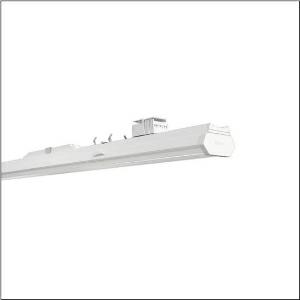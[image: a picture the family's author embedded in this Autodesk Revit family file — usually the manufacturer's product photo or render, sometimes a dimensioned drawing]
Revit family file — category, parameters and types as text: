
# Revit family: licross_r__11_protected_mo_51td11dn495g_7274
name_source: partatom
category: Lighting Fixtures
units: mm (PartAtom-declared; Revit-internal decimal feet)

## family parameters
Cut with Voids When Loaded = No
Host = Face
Light Source = No
Part Type = Normal
Room Calculation Point = No
Round Connector Dimension = Use Diameter
Shared = No

## types (1)
- --- (1 x LED, 9930 lm, 57.1 W, 4000K)
    Apparent Load = 57 VA
    CIE Flux Codes = 83 94 98 100 100
    Color Rendering = 80
    Color Temperature = 4000K
    Default Elevation = 1800 mm
    Description = Licross® 11 Protected MO, luminaire insert, of sheet steel, galvanised, coil coated, white, length: 1.500mm, width: 90mm, height: 101mm, LED rated luminous flux: 9.930lm, light colour: 840, control gear: DALI 2, control gear: ECG DALI, with plug, 5-pole, with phase selection, mains connection: 220..240V, AC, 50/60Hz, halogen-free wiring, primary light control with lens, of plastic, primary optical cover: cover, of PMMA, light emission: direct with ceiling illumination distribution, primary light characteristic: symmetric, protection rating (complete): IP54, insulation class (complete): insulation class I (protective earthing), certification: CE, ENEC, VDE, UKCA, protection symbol: D if used in an environment with non-conductive dust loads with corresponding accessories, impact resistance: IK06, permissible ambient temperature for indoor applications: -25..+35°C, corresponds to IFS (International Featured Standards) requirements for safety and quality in the food industry, reducing of maximum allowable ambient temperature of 5°C with ceiling mounting, LABS conformity tested according to VDMA 24364:2018-05, packaging unit: 1 piece
    Height = 92 mm
    Lamp = 1 x LED
    Lamp Light Flux = 9930 lm
    Lamp Power = 57.1 W
    Lamp count = 1
    Length = 1500 mm
    Luminous efficacy = 174 lm/W
    Manufacturer = Siteco
    ModVariant = No
    Model = 51TD11DN495G
    Mounting Place = Ceiling
    Mounting Type = Pendant
    Number of Poles = 1
    OnlyDefault = Yes
    Power Factor = 1
    Product Name = Licross® 11 Protected MO
    Product group = luminaire insert
    ProductGroupID = 902
    Protection Class = Protection class I
    Protection Degree = IP 54
    RLX_Detail_Level = 1
    RlxData = <blob elided: 24257 chars, md5=0099ae8f>
    Socket = socket
    Standby Power = 0 W
    System Light Flux = 9930 lm
    System Power = 57 W
    Type Comments = factory setting: luminous flux: 100 % | dim-lin: 254 | 378 mA
    Type Image = l_1256145.jpg
    URL = http://relux.com
    VarID = @adj_010123
    Voltage = 0 V
    Weight = 0.00 kg
    Width = 88 mm

## geometry (parser evidence)
native form markers: Blend x4, Sweep x12
no freeform markers — native parametric forms only
